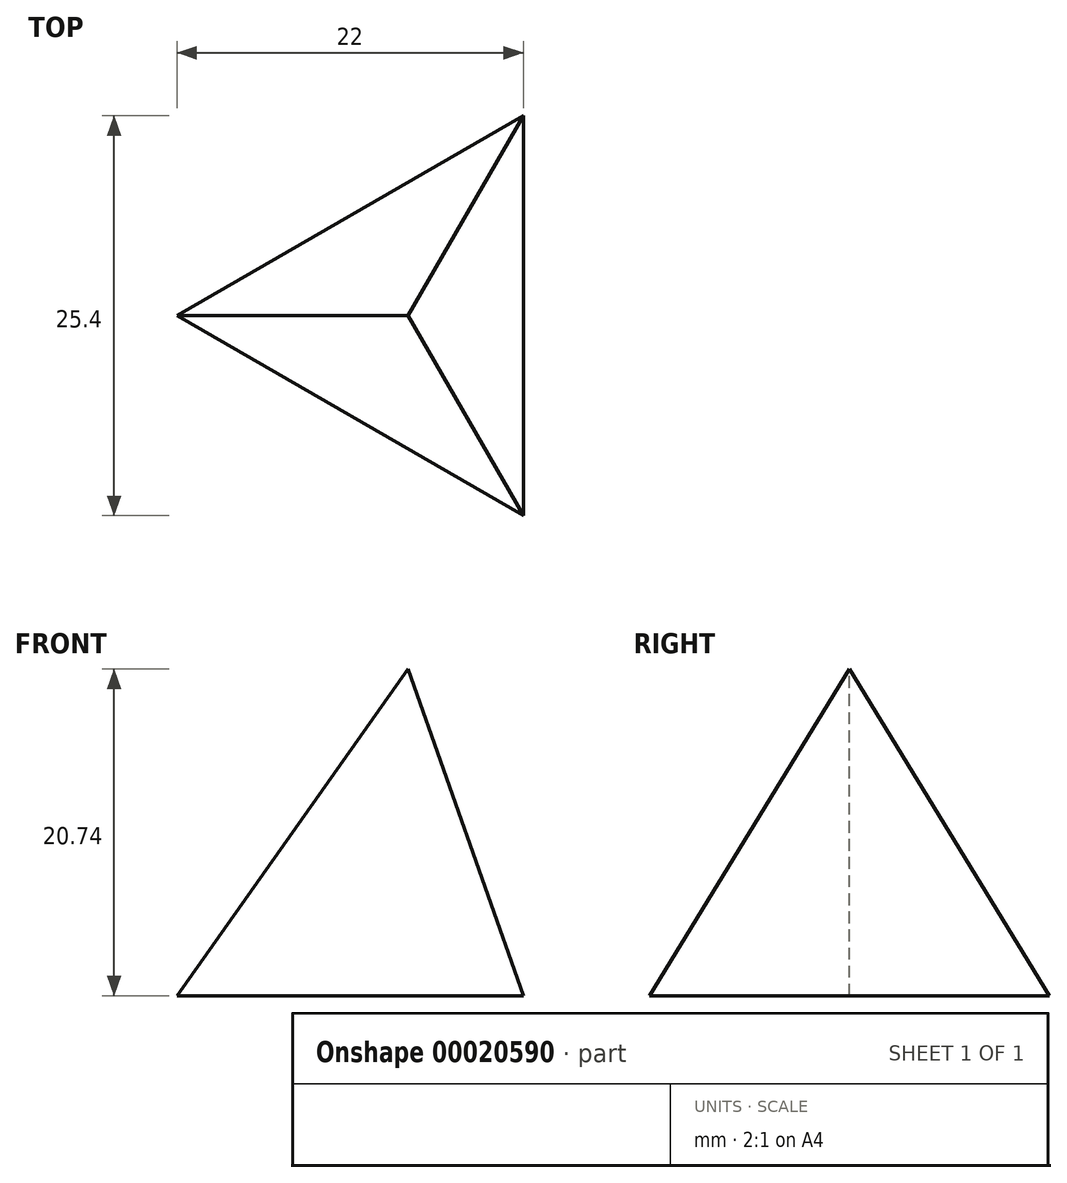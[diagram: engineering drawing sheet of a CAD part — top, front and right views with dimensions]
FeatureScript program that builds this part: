
annotation { "Feature Type Name" : "Feature", "Feature Type Description" : "" }
export const myFeature = defineFeature(function(context is Context, id is Id, definition is map)
    precondition{}
    {
        {
            var Q0;
            Q0=qCreatedBy(makeId("Top.planeOp"),FACE);
            var sketch = newSketch(context, id + "F0", { "sketchPlane" : qUnion([Q0])});
            skLineSegment(sketch, "E0", {"start": v(0, 0) * mm, "end": v(0, 25.4) * mm});
            skLineSegment(sketch, "E1", {"start": v(0, 25.4) * mm, "end": v(-22, 12.7) * mm});
            skLineSegment(sketch, "E2", {"start": v(0, 0) * mm, "end": v(-22, 12.7) * mm});
            skLineSegment(sketch, "E3", {"start": v(0, 25.4) * mm, "end": v(-11, 6.35) * mm, "construction": true});
            skSolve(sketch);
        }
        {
            var Q0;
            Q0=makeQuery(id+"F0.imprint","IMPRINT",FACE,{"disambiguationData":[TD([[makeQuery(id+"F0.imprint","IMPRINT",EDGE,{"derivedFrom":sQuery(id+"F0.wireOp",EDGE,"E0")}),1.0]])]});
            extrude(context, id + "F1", {"entities" : qUnion([Q0]), "depth" : 20.74 * mm});
        }
        {
            var Q0;
            Q0=makeQuery(id+"F1.opExtrude","CAP_FACE",FACE,{"disambiguationData":[OSD([sQuery(id+"F0.wireOp",EDGE,"E0"),sQuery(id+"F0.wireOp",EDGE,"E1"),sQuery(id+"F0.wireOp",EDGE,"E2")])],"isStart":false});
            var sketch = newSketch(context, id + "F2", { "sketchPlane" : qUnion([Q0])});
            skPoint(sketch, "E4", {"position": v(-7.33, 12.7) * mm});
            skPoint(sketch, "E5.end.orphan", {"position": v(-11, 19.05) * mm});
            skPoint(sketch, "E6.start.orphan", {"position": v(0, 12.7) * mm});
            skPoint(sketch, "E7.start.orphan", {"position": v(-11, 6.35) * mm});
            skSolve(sketch);
        }
        {
            var Q1;
            Q1=makeQuery(id+"F1.opExtrude","CAP_FACE",FACE,{"disambiguationData":[OSD([sQuery(id+"F0.wireOp",EDGE,"E0"),sQuery(id+"F0.wireOp",EDGE,"E1"),sQuery(id+"F0.wireOp",EDGE,"E2")])],"isStart":true});
            var Q2;
            Q2=sQuery(id+"F2.wireOp",VERTEX,"E4");
            loft(context, id + "F3", {"sheetProfilesArray" : [{ "sheetProfileEntities" : qUnion([Q1]) }, { "sheetProfileEntities" : qUnion([Q2]) }]});
        }
        {
            var Q0;
            Q0=makeQuery(id+"F1.opExtrude","SWEPT_BODY",BODY,{"disambiguationData":[OSD([sQuery(id+"F0.wireOp",EDGE,"E0"),sQuery(id+"F0.wireOp",EDGE,"E1"),sQuery(id+"F0.wireOp",EDGE,"E2")])]});
            deleteBodies(context, id + "F4", {"entities" : qUnion([Q0])});
        }
    });
